# Revit family: PRD_FrankeWS_WlMntdBbTps_WallOutlet_AQRM908
name_source: partatom
category: Plumbing Fixtures
revit_build: Autodesk Revit 2018 (Build: 20190510_1515(x64)
units: mm (PartAtom-declared; Revit-internal decimal feet)

## family parameters
Cut with Voids When Loaded = Yes
Host = Face
OmniClass Number = 23.45.55.14
OmniClass Title = Single Faucets
Part Type = Normal
Room Calculation Point = No
Round Connector Dimension = Use Diameter
Shared = Yes

## types (1)
- AQRM908
    AssetType = Fixed
    BIMObjectName = PRD_AR_WallMountedBibTaps_WallOutlet_AQRM908
    Category = Pr_40_20_87_93, Wall-mounted bib taps
    Color = Chrome
    Default Elevation = 2000 mm  [stored 6.56168 ft]
    Description = Wall outlet, DN 15, with aerator and rosette, polished chromium-plated brass, projection 75 mm.
    DiameterNominal = 15  [stored 0.0492126 ft]
    DurationUnit = year
    FaucetFunction = Mixed
    FaucetOperation = QuickAction
    FaucetType = Bib
    Features = polished chromium-plated brass
    Finish = polished chromium-plated
    Flow = 0.1 L/s
    GrossWeight = 0.50 kg
    IfcExportAs = IfcValveType
    IfcExportType = FAUCET
    Manufacturer = KWC Group AG
    ManufacturerName = KWC Group AG
    ManufacturerURL = www.kwc.com
    Material = Brass
    Model = AQRM908
    ModelNumber = 2000101048
    ModelReference = AQRM908
    NBSDescription = Taps and water supply fittings for sinks
    NBSReference = 45-35-70/345
    Name = Wall Outlet AQRM908
    NetWeight = 0.49 kg
    NominalDepth = 0 mm  [stored 0 ft]
    NominalHeight = 55 mm  [stored 0.180446 ft]
    NominalWidth = 55 mm  [stored 0.180446 ft]
    ProductCode = 208.0637.677
    ProductInformation = https://pim.kwc.com
    ShowerMaterial = PRD_AR_ChromatedBrass_HighPolished
    SpoutProjection = 75.00 mm
    TypeOfSpout = Wall outlet
    URL = www.kwc.com
    Uniclass2015Code = Pr_40_20_87_93
    Uniclass2015Title = Wall-mounted bib taps
    Uniclass2015Version = Products v1.23
    Version = 1
    VolumeFlowRate = 0.10 L/s at 3 bar
    WarrantyDurationUnit = year

note: [stored X ft] marks values corroborated as IEEE doubles in the binary element streams (Revit-internal decimal feet)

## geometry (parser evidence)
native form markers: Sweep x2
no freeform markers — native parametric forms only
